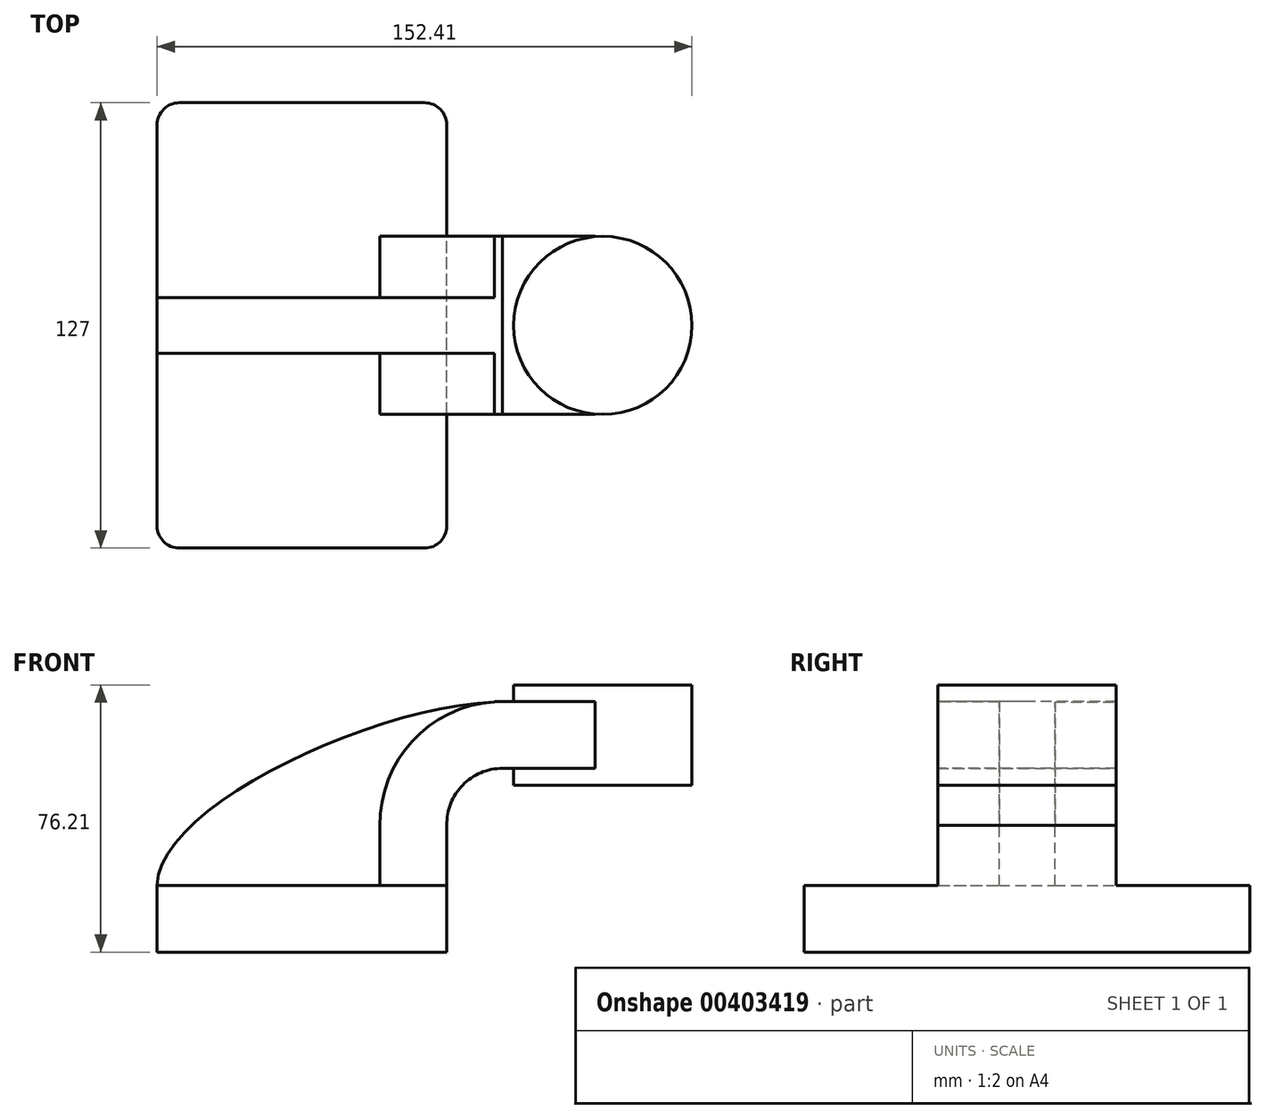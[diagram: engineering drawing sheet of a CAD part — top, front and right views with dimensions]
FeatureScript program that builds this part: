
annotation { "Feature Type Name" : "Feature", "Feature Type Description" : "" }
export const myFeature = defineFeature(function(context is Context, id is Id, definition is map)
    precondition{}
    {
        {
            var Q0;
            Q0=qCreatedBy(makeId("Front.planeOp"),FACE);
            var sketch = newSketch(context, id + "F0", { "sketchPlane" : qUnion([Q0])});
            skLineSegment(sketch, "E0.bottom", {"start": v(41.28, -9.52) * mm, "end": v(-41.28, -9.53) * mm});
            skLineSegment(sketch, "E0.top", {"start": v(41.28, 9.53) * mm, "end": v(-41.28, 9.53) * mm});
            skLineSegment(sketch, "E0.left", {"start": v(41.28, -9.52) * mm, "end": v(41.28, 9.53) * mm});
            skLineSegment(sketch, "E0.right", {"start": v(-41.28, -9.53) * mm, "end": v(-41.28, 9.53) * mm});
            skPoint(sketch, "E0.middle", {"position": v(0, 0) * mm});
            skLineSegment(sketch, "E1.bottom", {"start": v(111.12, 38.1) * mm, "end": v(60.33, 38.1) * mm});
            skLineSegment(sketch, "E1.top", {"start": v(111.12, 66.68) * mm, "end": v(60.33, 66.68) * mm});
            skLineSegment(sketch, "E1.left", {"start": v(111.12, 38.1) * mm, "end": v(111.12, 66.68) * mm});
            skLineSegment(sketch, "E1.right", {"start": v(60.33, 38.1) * mm, "end": v(60.33, 66.68) * mm});
            skPoint(sketch, "E1.middle", {"position": v(85.72, 52.39) * mm});
            skLineSegment(sketch, "E2", {"start": v(41.28, 9.53) * mm, "end": v(41.28, 26.63) * mm});
            skArc(sketch, "E3", {"start": v(41.28, 26.63) * mm, "mid": v(45.8, 38.1) * mm, "end": v(57.15, 42.88) * mm});
            skLineSegment(sketch, "E4", {"start": v(57.15, 42.88) * mm, "end": v(83.54, 42.88) * mm});
            skLineSegment(sketch, "E5.0", {"start": v(57.15, 61.93) * mm, "end": v(83.54, 61.93) * mm});
            skArc(sketch, "E5.1", {"start": v(22.22, 26.45) * mm, "mid": v(32.26, 51.5) * mm, "end": v(57.15, 61.93) * mm});
            skLineSegment(sketch, "E5.2", {"start": v(22.22, 9.53) * mm, "end": v(22.22, 26.45) * mm});
            skLineSegment(sketch, "E6", {"start": v(83.54, 42.88) * mm, "end": v(83.54, 61.93) * mm});
            skFitSpline(sketch, "E7", {"points": [v(-41.28, 9.53) * mm, v(57.15, 61.93) * mm], "startDerivative": vector(0.94, 68.37) * mm, "endDerivative": vector(107.05, 1.79) * mm});
            skLineSegment(sketch, "E8", {"start": v(85.72, 38.1) * mm, "end": v(85.72, 66.68) * mm});
            skSolve(sketch);
        }
        {
            var Q0;
            Q0=makeQuery(id+"F0.imprint","IMPRINT",FACE,{"disambiguationData":[TD([[makeQuery(id+"F0.imprint","IMPRINT",EDGE,{"derivedFrom":sQuery(id+"F0.wireOp",EDGE,"E0.bottom")}),-1.0]])]});
            extrude(context, id + "F1", {"entities" : qUnion([Q0]), "endBound" : BoundingType.SYMMETRIC, "depth" : 127 * mm});
        }
        {
            var Q0;
            {var subQ1=sQuery(id+"F0.wireOp",EDGE,"E2");Q0=makeQuery(id+"F0.imprint","IMPRINT",FACE,{"disambiguationData":[TD([[makeQuery(id+"F0.imprint","IMPRINT",EDGE,{"derivedFrom":subQ1}),1.0]])]});}
            var Q1;
            {var subQ5=sQuery(id+"F0.wireOp",EDGE,"E6");Q1=makeQuery(id+"F0.imprint","IMPRINT",FACE,{"disambiguationData":[TD([[makeQuery(id+"F0.imprint","IMPRINT",EDGE,{"derivedFrom":subQ5}),1.0]])]});}
            extrude(context, id + "F2", {"entities" : qUnion([Q0, Q1]), "operationType" : NewBodyOperationType.ADD, "endBound" : BoundingType.SYMMETRIC, "depth" : 50.8 * mm});
        }
        {
            var Q0;
            {var subQ3=sQuery(id+"F0.wireOp",EDGE,"E5.2");Q0=makeQuery(id+"F0.imprint","IMPRINT",FACE,{"disambiguationData":[TD([[makeQuery(id+"F0.imprint","IMPRINT",EDGE,{"derivedFrom":subQ3}),1.0]])]});}
            extrude(context, id + "F3", {"entities" : qUnion([Q0]), "operationType" : NewBodyOperationType.ADD, "endBound" : BoundingType.SYMMETRIC, "depth" : 15.88 * mm});
        }
        {
            var Q0;
            {var subQ0=sQuery(id+"F0.wireOp",EDGE,"E1.left");Q0=makeQuery(id+"F0.imprint","IMPRINT",FACE,{"disambiguationData":[TD([[makeQuery(id+"F0.imprint","IMPRINT",EDGE,{"derivedFrom":subQ0}),1.0]])]});}
            var Q1;
            Q1=sQuery(id+"F0.wireOp",EDGE,"E8");
            revolve(context, id + "F4", {"operationType" : NewBodyOperationType.ADD, "entities" : qUnion([Q0]), "axis" : qUnion([Q1]), "revolveType" : RevolveType.FULL});
        }
        {
            var Q0;
            Q0=makeQuery(id+"F1.opExtrude","CAP_EDGE",EDGE,{"disambiguationData":[OSD([sQuery(id+"F0.wireOp",EDGE,"E0.right")])],"isStart":false});
            var Q1;
            Q1=makeQuery(id+"F1.opExtrude","CAP_EDGE",EDGE,{"disambiguationData":[OSD([sQuery(id+"F0.wireOp",EDGE,"E0.left")])],"isStart":false});
            var Q2;
            Q2=makeQuery(id+"F1.opExtrude","CAP_EDGE",EDGE,{"disambiguationData":[OSD([sQuery(id+"F0.wireOp",EDGE,"E0.left")])],"isStart":true});
            var Q3;
            Q3=makeQuery(id+"F1.opExtrude","CAP_EDGE",EDGE,{"disambiguationData":[OSD([sQuery(id+"F0.wireOp",EDGE,"E0.right")])],"isStart":true});
            fillet(context, id + "F5", {"entities" : qUnion([Q0, Q1, Q2, Q3]), "radius" : 6.35 * mm, "tangentPropagation" : true, "allowEdgeOverflow" : false});
        }
    });
